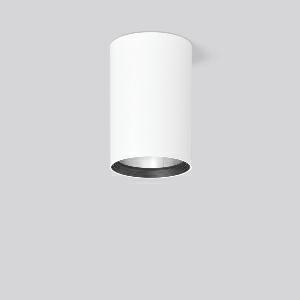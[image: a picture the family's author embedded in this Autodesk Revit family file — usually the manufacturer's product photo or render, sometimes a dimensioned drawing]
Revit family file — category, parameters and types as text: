
# Revit family: heledon_maxi_a_931223_002_3_76_e9ea
name_source: partatom
category: Lighting Fixtures
units: mm (PartAtom-declared; Revit-internal decimal feet)

## family parameters
Cut with Voids When Loaded = No
Host = Face
Light Source = No
Part Type = Normal
Room Calculation Point = No
Round Connector Dimension = Use Diameter
Shared = No

## types (1)
- HELEDON maxi A (1 x LED Modul 935, 4250 lm, 3500)
    Apparent Load = 35 VA
    Approval mark = CE
    CIE Flux Codes = 100 100 100 100 100
    Color Rendering = 92
    Color Temperature = 3500
    Default Elevation = 1800 mm
    Description = Series: HELEDON maxi
Cylindrical surface-mounted downlight. Housing: die-cast aluminium, powder-coated. Internal ceiling frame polycarbonate with bayonet mounting. Black plastic ring and recessed LED to prevent glare from the side. Optical assembly with reflector made of MIRO-Silver with 98% total light reflection for outstanding efficiency - can be changed without tools. Best colour rendering index Ra>90. Suitable for Ceiling mounting. Easy installation with a separate ceiling frame with bayonet mounting and plug connection. Driver integrated. Connected via plug-in connector. High quality converter without flickering and stroboscopic effect. The following accessories can be mounted without use of tools: interchangeable lenses, decorative glasses, honeycomb louvre, clear and frosted diffusers, white interchangeable plastic ring. 
Colour: traffic white, matt (RAL 9016)
Diameter: 123 mm
Height: 183 mm
Lamp: LED
Socket: without socket
Colour temperature: 3500K
Colour rendering index (CRI): 92
System power: 35 W
Rated luminous flux: 4250 lm
Luminous efficiency: 121 lm/W
Control gear: Converter, dimmable, DALI
Protection class: I
Type of protection: IP 20
    Height = 183 mm
    Lamp = 1 x LED Modul 935
    Lamp Light Flux = 4250 lm
    Lamp count = 1
    Length = 123 mm
    Lifetime = 50000 h
    Luminous efficacy = 121 lm/W
    Manufacturer = RZB
    ModVariant = No
    Model = 931223.002.3.76
    Mounting Place = Ceiling
    Mounting Type = Surface mounted
    Number of Poles = 1
    OnlyDefault = Yes
    Power Factor = 1
    Product Name = HELEDON maxi A
    Product group = Surface mounted downlights
    ProductGroupID = 302
    Protection Class = Protection class I
    Protection Degree = IP 20
    RLX_Detail_Level = 1
    RLX_Emergency_Light_Flux = 0 lm
    RLX_Emergency_Type = 0
    RLX_Emergency_Type_DB = No
    RlxData = <blob elided: 98821 chars, md5=97cd7607>
    Socket = socket
    Standby Power = 0 W
    System Light Flux = 4250 lm
    System Power = 35 W
    Type Comments = Product without accessories
    Type Image = 931192.002.jpg
    URL = http://relux.com
    VarID = ---
    Voltage = 230 V
    Voltage Range = 220-240 V
    Weight = 0.00 kg
    Width = 0 mm  [stored 0 ft]

note: [stored X ft] marks values corroborated as IEEE doubles in the binary element streams (Revit-internal decimal feet)

## geometry (parser evidence)
native form markers: Blend x4, Sweep x11
no freeform markers — native parametric forms only
